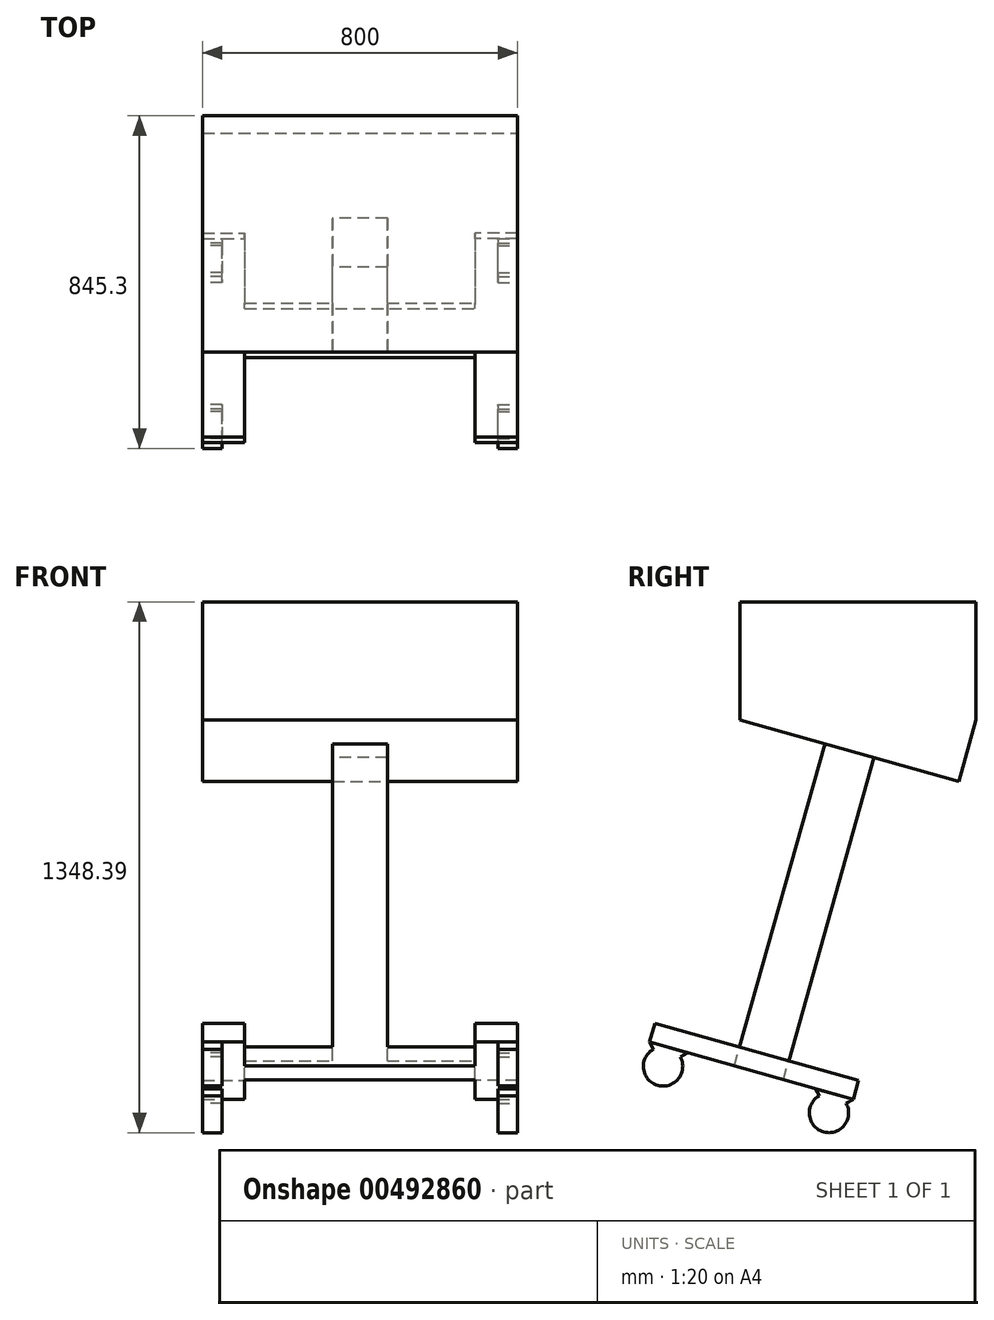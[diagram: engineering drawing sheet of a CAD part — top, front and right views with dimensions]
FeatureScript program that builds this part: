
annotation { "Feature Type Name" : "Feature", "Feature Type Description" : "" }
export const myFeature = defineFeature(function(context is Context, id is Id, definition is map)
    precondition{}
    {
        {
            var Q0;
            Q0=qCreatedBy(makeId("Top.planeOp"),FACE);
            var sketch = newSketch(context, id + "F0", { "sketchPlane" : qUnion([Q0])});
            skLineSegment(sketch, "E0.bottom", {"start": v(0, 0) * mm, "end": v(800, 0) * mm});
            skLineSegment(sketch, "E0.top", {"start": v(0, 600) * mm, "end": v(800, 600) * mm});
            skLineSegment(sketch, "E0.left", {"start": v(0, 0) * mm, "end": v(0, 600) * mm});
            skLineSegment(sketch, "E0.right", {"start": v(800, 0) * mm, "end": v(800, 600) * mm});
            skSolve(sketch);
        }
        {
            var Q0;
            Q0 = qSketchRegion(id + "F0", true);
            extrude(context, id + "F1", {"entities" : qUnion([Q0]), "depth" : 300 * mm});
        }
        {
            var Q0;
            Q0=makeQuery(id+"F1.opExtrude","SWEPT_FACE",FACE,{"disambiguationData":[OSD([sQuery(id+"F0.wireOp",EDGE,"E0.right")])]});
            var sketch = newSketch(context, id + "F2", { "sketchPlane" : qUnion([Q0])});
            skLineSegment(sketch, "E1", {"start": v(0, 0) * mm, "end": v(600, 0) * mm});
            skLineSegment(sketch, "E2", {"start": v(600, 0) * mm, "end": v(556.1, -156.24) * mm});
            skLineSegment(sketch, "E3", {"start": v(556.1, -156.24) * mm, "end": v(0, 0) * mm});
            skSolve(sketch);
        }
        {
            var Q0;
            Q0=makeQuery(id+"F2.imprint","IMPRINT",FACE,{"disambiguationData":[TD([[makeQuery(id+"F2.imprint","IMPRINT",EDGE,{"derivedFrom":sQuery(id+"F2.wireOp",EDGE,"E1")}),-1.0]])]});
            extrude(context, id + "F3", {"entities" : qUnion([Q0]), "operationType" : NewBodyOperationType.ADD, "oppositeDirection" : true, "depth" : 800 * mm});
        }
        {
            var Q0;
            Q0=makeQuery(id+"F3.opExtrude","SWEPT_FACE",FACE,{"disambiguationData":[OSD([sQuery(id+"F2.wireOp",EDGE,"E3")])]});
            var sketch = newSketch(context, id + "F4", { "sketchPlane" : qUnion([Q0])});
            skPoint(sketch, "E4.firstSnap0", {"position": v(0, -288.82) * mm});
            skPoint(sketch, "E4.firstSnap1", {"position": v(400, 0) * mm});
            skLineSegment(sketch, "E4.top", {"start": v(400, -224.02) * mm, "end": v(330.51, -224.02) * mm});
            skLineSegment(sketch, "E4.right", {"start": v(330.51, -288.82) * mm, "end": v(330.51, -224.02) * mm});
            skLineSegment(sketch, "E5", {"start": v(400, 0) * mm, "end": v(400, -577.63) * mm});
            skLineSegment(sketch, "E6", {"start": v(0, -288.82) * mm, "end": v(800, -288.82) * mm});
            skLineSegment(sketch, "E7.MirrorCS", {"start": v(400, -224.02) * mm, "end": v(469.49, -224.02) * mm});
            skLineSegment(sketch, "E8.MirrorCS", {"start": v(469.49, -288.82) * mm, "end": v(469.49, -224.02) * mm});
            skLineSegment(sketch, "E9.MirrorCS", {"start": v(330.51, -288.82) * mm, "end": v(330.51, -353.61) * mm});
            skLineSegment(sketch, "E10.MirrorCS", {"start": v(400, -353.61) * mm, "end": v(330.51, -353.61) * mm});
            skLineSegment(sketch, "E11.MirrorCS", {"start": v(400, -353.61) * mm, "end": v(469.49, -353.61) * mm});
            skLineSegment(sketch, "E12.MirrorCS", {"start": v(469.49, -288.82) * mm, "end": v(469.49, -353.61) * mm});
            skSolve(sketch);
        }
        {
            var Q0;
            Q0 = qSketchRegion(id + "F4", true);
            extrude(context, id + "F5", {"entities" : qUnion([Q0]), "operationType" : NewBodyOperationType.ADD, "depth" : 800 * mm});
        }
        {
            var Q0;
            Q0=makeQuery(id+"F5.opExtrude","CAP_FACE",FACE,{"disambiguationData":[OSD([sQuery(id+"F4.wireOp",EDGE,"E4.top"),sQuery(id+"F4.wireOp",EDGE,"E4.right"),sQuery(id+"F4.wireOp",EDGE,"E7.MirrorCS"),sQuery(id+"F4.wireOp",EDGE,"E8.MirrorCS"),sQuery(id+"F4.wireOp",EDGE,"E9.MirrorCS"),sQuery(id+"F4.wireOp",EDGE,"E10.MirrorCS"),sQuery(id+"F4.wireOp",EDGE,"E11.MirrorCS"),sQuery(id+"F4.wireOp",EDGE,"E12.MirrorCS")])],"isStart":false});
            var sketch = newSketch(context, id + "F6", { "sketchPlane" : qUnion([Q0])});
            skLineSegment(sketch, "E13", {"start": v(0, 0) * mm, "end": v(0, -537.79) * mm});
            skLineSegment(sketch, "E14", {"start": v(0, -537.79) * mm, "end": v(107.34, -537.79) * mm});
            skLineSegment(sketch, "E15", {"start": v(107.34, -537.79) * mm, "end": v(107.34, -353.61) * mm});
            skLineSegment(sketch, "E16", {"start": v(107.34, -353.61) * mm, "end": v(330.51, -353.61) * mm});
            skLineSegment(sketch, "E17", {"start": v(0, 0) * mm, "end": v(107.34, 0) * mm});
            skLineSegment(sketch, "E18", {"start": v(107.34, 0) * mm, "end": v(107.34, -224.02) * mm});
            skLineSegment(sketch, "E19", {"start": v(107.34, -224.02) * mm, "end": v(330.51, -224.02) * mm});
            skLineSegment(sketch, "E20", {"start": v(330.51, -224.02) * mm, "end": v(400, -224.02) * mm});
            skLineSegment(sketch, "E21", {"start": v(400, -224.02) * mm, "end": v(400, -353.61) * mm});
            skLineSegment(sketch, "E22", {"start": v(400, -353.61) * mm, "end": v(330.51, -353.61) * mm});
            skLineSegment(sketch, "E23.MirrorCS", {"start": v(400, -353.61) * mm, "end": v(469.49, -353.61) * mm});
            skLineSegment(sketch, "E24.MirrorCS", {"start": v(469.49, -224.02) * mm, "end": v(400, -224.02) * mm});
            skLineSegment(sketch, "E25.MirrorCS", {"start": v(692.66, -224.02) * mm, "end": v(469.49, -224.02) * mm});
            skLineSegment(sketch, "E26.MirrorCS", {"start": v(692.66, -353.61) * mm, "end": v(469.49, -353.61) * mm});
            skLineSegment(sketch, "E27.MirrorCS", {"start": v(692.66, -537.79) * mm, "end": v(692.66, -353.61) * mm});
            skLineSegment(sketch, "E28.MirrorCS", {"start": v(800, -537.79) * mm, "end": v(692.66, -537.79) * mm});
            skLineSegment(sketch, "E29.MirrorCS", {"start": v(800, 0) * mm, "end": v(800, -537.79) * mm});
            skLineSegment(sketch, "E30.MirrorCS", {"start": v(800, 0) * mm, "end": v(692.66, 0) * mm});
            skLineSegment(sketch, "E31.MirrorCS", {"start": v(692.66, 0) * mm, "end": v(692.66, -224.02) * mm});
            skSolve(sketch);
        }
        {
            var Q0;
            Q0 = qSketchRegion(id + "F6", true);
            extrude(context, id + "F7", {"entities" : qUnion([Q0]), "operationType" : NewBodyOperationType.ADD, "depth" : 50 * mm});
        }
        {
            var Q0;
            Q0=makeQuery(id+"F7.opExtrude","SWEPT_FACE",FACE,{"disambiguationData":[OSD([sQuery(id+"F6.wireOp",EDGE,"E13")])]});
            var sketch = newSketch(context, id + "F8", { "sketchPlane" : qUnion([Q0])});
            skLineSegment(sketch, "E32", {"start": v(229.91, -818.31) * mm, "end": v(133.64, -845.36) * mm});
            skLineSegment(sketch, "E33", {"start": v(181.78, -831.84) * mm, "end": v(195.3, -879.98) * mm});
            skLineSegment(sketch, "E34", {"start": v(-28.96, -891.05) * mm, "end": v(-42.48, -842.91) * mm});
            skLineSegment(sketch, "E35", {"start": v(229.91, -818.31) * mm, "end": v(195.3, -879.98) * mm});
            skLineSegment(sketch, "E36", {"start": v(133.64, -845.36) * mm, "end": v(195.3, -879.98) * mm});
            skCircle(sketch, "E37", {"center": v(195.3, -879.98) * mm, "radius": 50 * mm});
            skLineSegment(sketch, "E38.MirrorCS", {"start": v(-287.83, -963.78) * mm, "end": v(-226.16, -998.4) * mm});
            skCircle(sketch, "E39.MirrorC", {"center": v(-226.16, -998.4) * mm, "radius": 50 * mm});
            skLineSegment(sketch, "E40.MirrorCS", {"start": v(-191.55, -936.73) * mm, "end": v(-226.16, -998.4) * mm});
            skLineSegment(sketch, "E41.MirrorCS", {"start": v(-287.83, -963.78) * mm, "end": v(-191.55, -936.73) * mm});
            skSolve(sketch);
        }
        {
            var Q0;
            Q0 = qSketchRegion(id + "F8", true);
            extrude(context, id + "F9", {"entities" : qUnion([Q0]), "operationType" : NewBodyOperationType.ADD, "oppositeDirection" : true, "depth" : 50 * mm});
        }
        {
            var Q0;
            Q0=makeQuery(id+"F7.opExtrude","SWEPT_FACE",FACE,{"disambiguationData":[OSD([sQuery(id+"F6.wireOp",EDGE,"E29.MirrorCS")])]});
            var sketch = newSketch(context, id + "F10", { "sketchPlane" : qUnion([Q0])});
            skLineSegment(sketch, "E42", {"start": v(287.83, -963.78) * mm, "end": v(191.55, -936.73) * mm});
            skLineSegment(sketch, "E43", {"start": v(28.96, -891.05) * mm, "end": v(42.48, -842.91) * mm});
            skLineSegment(sketch, "E44", {"start": v(239.69, -950.26) * mm, "end": v(226.16, -998.4) * mm});
            skLineSegment(sketch, "E45", {"start": v(191.55, -936.73) * mm, "end": v(226.16, -998.4) * mm});
            skLineSegment(sketch, "E46", {"start": v(287.83, -963.78) * mm, "end": v(226.16, -998.4) * mm});
            skCircle(sketch, "E47", {"center": v(226.16, -998.4) * mm, "radius": 50 * mm});
            skCircle(sketch, "E48.MirrorC", {"center": v(-195.3, -879.98) * mm, "radius": 50 * mm});
            skLineSegment(sketch, "E49.MirrorCS", {"start": v(-133.64, -845.36) * mm, "end": v(-195.3, -879.98) * mm});
            skLineSegment(sketch, "E50.MirrorCS", {"start": v(-229.91, -818.31) * mm, "end": v(-195.3, -879.98) * mm});
            skLineSegment(sketch, "E51.MirrorCS", {"start": v(-229.91, -818.31) * mm, "end": v(-133.64, -845.36) * mm});
            skSolve(sketch);
        }
        {
            var Q0;
            Q0 = qSketchRegion(id + "F10", true);
            extrude(context, id + "F11", {"entities" : qUnion([Q0]), "oppositeDirection" : true, "depth" : 50 * mm});
        }
    });
